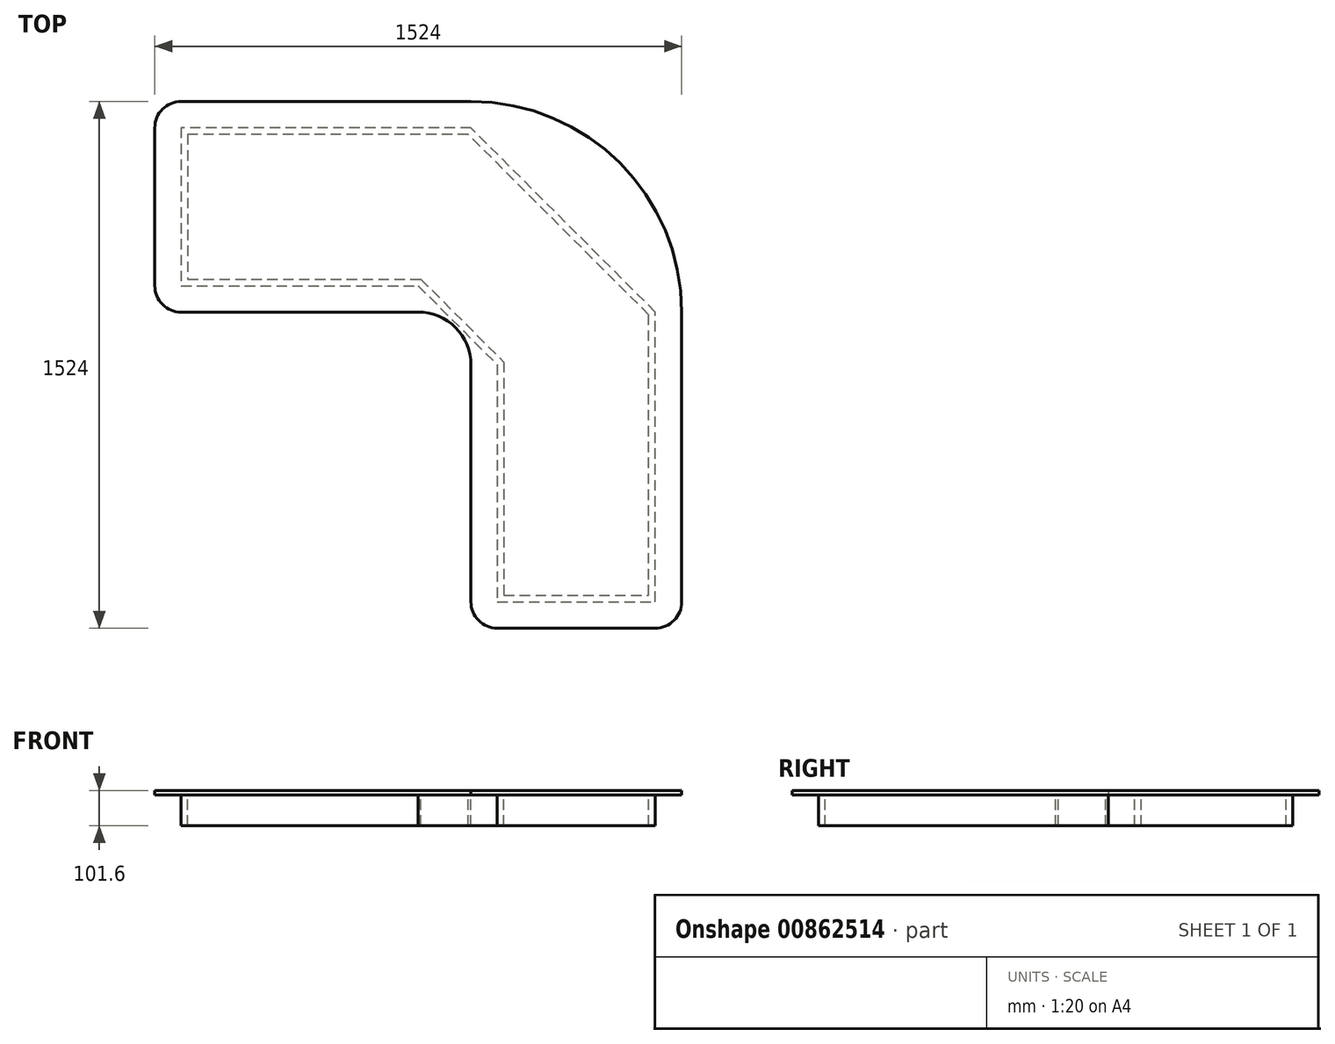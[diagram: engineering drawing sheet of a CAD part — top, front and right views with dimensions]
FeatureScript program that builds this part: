
annotation { "Feature Type Name" : "Feature", "Feature Type Description" : "" }
export const myFeature = defineFeature(function(context is Context, id is Id, definition is map)
    precondition{}
    {
        {
            var Q0;
            Q0=qCreatedBy(makeId("Top.planeOp"),FACE);
            var sketch = newSketch(context, id + "F0", { "sketchPlane" : qUnion([Q0])});
            skLineSegment(sketch, "E0.bottom", {"start": v(-431.05, 0) * mm, "end": v(-1955.05, 0) * mm, "construction": true});
            skLineSegment(sketch, "E0.top", {"start": v(-431.05, 558.8) * mm, "end": v(-1955.05, 558.8) * mm, "construction": true});
            skLineSegment(sketch, "E0.left", {"start": v(-431.05, 0) * mm, "end": v(-431.05, 558.8) * mm, "construction": true});
            skLineSegment(sketch, "E0.right", {"start": v(-1955.05, 0) * mm, "end": v(-1955.05, 558.8) * mm, "construction": true});
            skLineSegment(sketch, "E1.bottom", {"start": v(0, -431.05) * mm, "end": v(558.8, -431.05) * mm, "construction": true});
            skLineSegment(sketch, "E1.top", {"start": v(0, -1955.05) * mm, "end": v(558.8, -1955.05) * mm, "construction": true});
            skLineSegment(sketch, "E1.left", {"start": v(0, -431.05) * mm, "end": v(0, -1955.05) * mm, "construction": true});
            skLineSegment(sketch, "E1.right", {"start": v(558.8, -431.05) * mm, "end": v(558.8, -1955.05) * mm, "construction": true});
            skLineSegment(sketch, "E2", {"start": v(-431.05, 0) * mm, "end": v(0, -431.05) * mm, "construction": true});
            skArc(sketch, "E3", {"start": v(558.8, -431.05) * mm, "mid": v(268.88, 268.88) * mm, "end": v(-431.05, 558.8) * mm, "construction": true});
            skLineSegment(sketch, "E4", {"start": v(0, 0) * mm, "end": v(0, -431.05) * mm, "construction": true});
            skLineSegment(sketch, "E5", {"start": v(-431.05, 0) * mm, "end": v(0, 0) * mm, "construction": true});
            skLineSegment(sketch, "E6.bottom", {"start": v(-1878.85, -431.05) * mm, "end": v(-1040.65, -431.05) * mm});
            skLineSegment(sketch, "E6.top", {"start": v(-1878.85, -1040.65) * mm, "end": v(-1193.05, -1040.65) * mm});
            skLineSegment(sketch, "E6.left", {"start": v(-1955.05, -507.25) * mm, "end": v(-1955.05, -964.45) * mm});
            skLineSegment(sketch, "E6.right", {"start": v(-1040.65, -431.05) * mm, "end": v(-1040.65, -1040.65) * mm, "construction": true});
            skLineSegment(sketch, "E7.bottom", {"start": v(-1040.65, -1040.65) * mm, "end": v(-431.05, -1040.65) * mm, "construction": true});
            skLineSegment(sketch, "E7.top", {"start": v(-964.45, -1955.05) * mm, "end": v(-507.25, -1955.05) * mm});
            skLineSegment(sketch, "E7.left", {"start": v(-1040.65, -1193.05) * mm, "end": v(-1040.65, -1878.85) * mm});
            skLineSegment(sketch, "E7.right", {"start": v(-431.05, -1040.65) * mm, "end": v(-431.05, -1878.85) * mm});
            skArc(sketch, "E8", {"start": v(-1040.65, -431.05) * mm, "mid": v(-609.6, -609.6) * mm, "end": v(-431.05, -1040.65) * mm});
            skLineSegment(sketch, "E9", {"start": v(-1955.05, -431.05) * mm, "end": v(-1955.05, 0) * mm, "construction": true});
            skLineSegment(sketch, "E10", {"start": v(-431.05, -1955.05) * mm, "end": v(0, -1955.05) * mm, "construction": true});
            skArc(sketch, "E11.filletArc", {"start": v(-1040.65, -1193.05) * mm, "mid": v(-1085.29, -1085.29) * mm, "end": v(-1193.05, -1040.65) * mm});
            skPoint(sketch, "E12.visualSharp", {"position": v(-1955.05, -431.05) * mm});
            skArc(sketch, "E12.filletArc", {"start": v(-1878.85, -431.05) * mm, "mid": v(-1932.73, -453.37) * mm, "end": v(-1955.05, -507.25) * mm});
            skPoint(sketch, "E13.visualSharp", {"position": v(-1955.05, -1040.65) * mm});
            skArc(sketch, "E13.filletArc", {"start": v(-1955.05, -964.45) * mm, "mid": v(-1932.73, -1018.33) * mm, "end": v(-1878.85, -1040.65) * mm});
            skPoint(sketch, "E14.visualSharp", {"position": v(-431.05, -1955.05) * mm});
            skArc(sketch, "E14.filletArc", {"start": v(-507.25, -1955.05) * mm, "mid": v(-453.37, -1932.73) * mm, "end": v(-431.05, -1878.85) * mm});
            skPoint(sketch, "E15.visualSharp", {"position": v(-1040.65, -1955.05) * mm});
            skArc(sketch, "E15.filletArc", {"start": v(-1040.65, -1878.85) * mm, "mid": v(-1018.33, -1932.73) * mm, "end": v(-964.45, -1955.05) * mm});
            skSolve(sketch);
        }
        {
            var Q0;
            Q0=qSketchRegion(id+"F0",true);
            extrude(context, id + "F1", {"entities" : qUnion([Q0]), "depth" : 12.7 * mm, "offsetDistance" : 25.4 * mm});
        }
        {
            var Q0;
            Q0=makeQuery(id+"F1.opExtrude","CAP_FACE",FACE,{"disambiguationData":[OSD([sQuery(id+"F0.wireOp",EDGE,"E6.bottom"),sQuery(id+"F0.wireOp",EDGE,"E6.top"),sQuery(id+"F0.wireOp",EDGE,"E6.left"),sQuery(id+"F0.wireOp",EDGE,"E7.top"),sQuery(id+"F0.wireOp",EDGE,"E7.left"),sQuery(id+"F0.wireOp",EDGE,"E7.right"),sQuery(id+"F0.wireOp",EDGE,"E8"),sQuery(id+"F0.wireOp",EDGE,"E11.filletArc"),sQuery(id+"F0.wireOp",EDGE,"E12.filletArc"),sQuery(id+"F0.wireOp",EDGE,"E13.filletArc"),sQuery(id+"F0.wireOp",EDGE,"E14.filletArc"),sQuery(id+"F0.wireOp",EDGE,"E15.filletArc")])],"isStart":true});
            var sketch = newSketch(context, id + "F2", { "sketchPlane" : qUnion([Q0])});
            skLineSegment(sketch, "E16", {"start": v(-964.45, 1878.85) * mm, "end": v(-507.25, 1878.85) * mm});
            skLineSegment(sketch, "E17", {"start": v(-507.25, 1878.85) * mm, "end": v(-507.25, 1040.65) * mm});
            skLineSegment(sketch, "E18", {"start": v(-507.25, 1040.65) * mm, "end": v(-1040.65, 507.25) * mm});
            skLineSegment(sketch, "E19", {"start": v(-1040.65, 507.25) * mm, "end": v(-1878.85, 507.25) * mm});
            skLineSegment(sketch, "E20", {"start": v(-1878.85, 507.25) * mm, "end": v(-1878.85, 964.45) * mm});
            skLineSegment(sketch, "E21", {"start": v(-1878.85, 964.45) * mm, "end": v(-1193.05, 964.45) * mm});
            skLineSegment(sketch, "E22", {"start": v(-1193.05, 964.45) * mm, "end": v(-964.45, 1193.05) * mm});
            skLineSegment(sketch, "E23", {"start": v(-964.45, 1193.05) * mm, "end": v(-964.45, 1878.85) * mm});
            skLineSegment(sketch, "E24", {"start": v(-945.4, 1859.8) * mm, "end": v(-526.3, 1859.8) * mm});
            skLineSegment(sketch, "E25", {"start": v(-526.3, 1859.8) * mm, "end": v(-526.3, 1048.54) * mm});
            skLineSegment(sketch, "E26", {"start": v(-526.3, 1048.54) * mm, "end": v(-1048.54, 526.3) * mm});
            skLineSegment(sketch, "E27", {"start": v(-1048.54, 526.3) * mm, "end": v(-1859.8, 526.3) * mm});
            skLineSegment(sketch, "E28", {"start": v(-1859.8, 526.3) * mm, "end": v(-1859.8, 945.4) * mm});
            skLineSegment(sketch, "E29", {"start": v(-1859.8, 945.4) * mm, "end": v(-1185.16, 945.4) * mm});
            skLineSegment(sketch, "E30", {"start": v(-1185.16, 945.4) * mm, "end": v(-945.4, 1185.16) * mm});
            skLineSegment(sketch, "E31", {"start": v(-945.4, 1185.16) * mm, "end": v(-945.4, 1859.8) * mm});
            skSolve(sketch);
        }
        {
            var Q0;
            Q0 = qSketchRegion(id + "F2", true);
            extrude(context, id + "F3", {"entities" : qUnion([Q0]), "operationType" : NewBodyOperationType.ADD, "depth" : 88.9 * mm, "offsetDistance" : 25.4 * mm});
        }
    });
